AUTODESK INVENTOR PART (.ipt)
format: ipt  version: 2023 (Build 270158000, 158)  size: 282,112 bytes
history: native  units: mm
features: reference x7, other x5, extrude x4, fillet x3, plane x2, sketch x2, projected_geometry x1
ambient origin geometry x8: Origin, YZ Plane, XZ Plane, XY Plane, X Axis, Y Axis, Z Axis, Center Point
bodies: Solid1 (feature_tree)
feature tree (24):
  plane  "Work Plane1"
  sketch  "Sketch1"  dims[d0=2.014378mm d1=2.014378mm]
  extrude  "Extrusion1"  Depth=2.014378mm
  extrude  "Extrusion2"  Depth=5.0mm
  extrude  "Extrusion3"  TaperAngle=0.0deg  [1 undecoded]
  plane  "Work Plane2"
  sketch  "Sketch2"  dims[d2=10.0mm d3=5.0mm d5=0.0mm d6=3.0mm d7=30.0mm d8=0.0mm d9=28.0mm d10=0.0mm d11=5.0mm d12=0.0mm d13=3.0mm d14=57.35mm d15=0.0mm d16=1.0mm d17=3.0mm]
  fillet  "Fillet1"  Radius=3.0mm
  extrude  "Extrusion4"  Depth=30.0mm TaperAngle=0.0deg
  fillet  "Fillet2"  Radius=28.0mm
  fillet  "Fillet3"  Radius=5.0mm
  reference  "Reference1"
  reference  "Reference2"
  reference  "Reference3"
  reference  "Reference4"
  reference  "Reference5"
  reference  "Reference6"
  projected_geometry  "Projected Loop1"
  reference  "Reference7"
  parser-record x1  (decoder bookkeeping rows leaked as tree rows — omitted from the tree; the rows remain in map.json)
  other  "Assembly_V6.iam"
  other  "house_V6:1"
  other  "mouldingPlate_V6:1"
  other  "screw:1"
note: 1 required parameter value undecoded (feature->parameter linkage not recoverable at this tier; creation-order binding heuristic only, values carry confidence <= 0.55)
note: 1 file-system path scrubbed to <path> (originals preserved in map.json)
